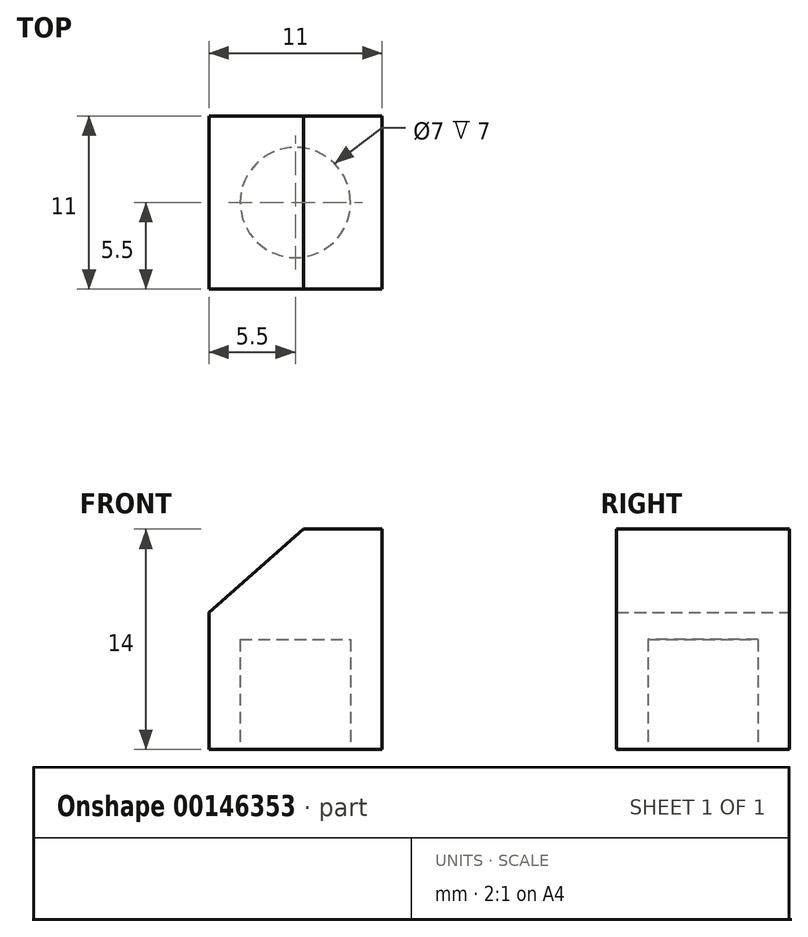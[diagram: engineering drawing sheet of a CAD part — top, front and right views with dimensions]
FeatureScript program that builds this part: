
annotation { "Feature Type Name" : "Feature", "Feature Type Description" : "" }
export const myFeature = defineFeature(function(context is Context, id is Id, definition is map)
    precondition{}
    {
        {
            var Q0;
            Q0=qCreatedBy(makeId("Front.planeOp"),FACE);
            var sketch = newSketch(context, id + "F0", { "sketchPlane" : qUnion([Q0])});
            skLineSegment(sketch, "E0.bottom", {"start": v(5.5, 7) * mm, "end": v(-5.5, 7) * mm});
            skLineSegment(sketch, "E0.top", {"start": v(5.5, -7) * mm, "end": v(-5.5, -7) * mm});
            skLineSegment(sketch, "E0.left", {"start": v(5.5, 7) * mm, "end": v(5.5, -7) * mm});
            skLineSegment(sketch, "E0.right", {"start": v(-5.5, 7) * mm, "end": v(-5.5, -7) * mm});
            skPoint(sketch, "E0.middle", {"position": v(0, 0) * mm});
            skLineSegment(sketch, "E1", {"start": v(0.5, 7) * mm, "end": v(-5.5, 1.7) * mm});
            skSolve(sketch);
        }
        {
            var Q0;
            {var subQ1=sQuery(id+"F0.wireOp",EDGE,"E0.top");Q0=makeQuery(id+"F0.imprint","IMPRINT",FACE,{"disambiguationData":[TD([[makeQuery(id+"F0.imprint","IMPRINT",EDGE,{"derivedFrom":subQ1}),-1.0]])]});}
            extrude(context, id + "F1", {"entities" : qUnion([Q0]), "endBound" : BoundingType.SYMMETRIC, "depth" : 11 * mm});
        }
        {
            var Q0;
            Q0=makeQuery(id+"F1.opExtrude","SWEPT_FACE",FACE,{"disambiguationData":[OSD([sQuery(id+"F0.wireOp",EDGE,"E0.top")])]});
            var sketch = newSketch(context, id + "F2", { "sketchPlane" : qUnion([Q0])});
            skCircle(sketch, "E2", {"center": v(0, 0) * mm, "radius": 3.5 * mm});
            skSolve(sketch);
        }
        {
            var Q0;
            Q0=makeQuery(id+"F2.imprint","IMPRINT",FACE,{"disambiguationData":[TD([[makeQuery(id+"F2.imprint","IMPRINT",EDGE,{"derivedFrom":sQuery(id+"F2.wireOp",EDGE,"E2")}),1.0]])]});
            extrude(context, id + "F3", {"entities" : qUnion([Q0]), "operationType" : NewBodyOperationType.REMOVE, "oppositeDirection" : true, "depth" : 7 * mm});
        }
    });
